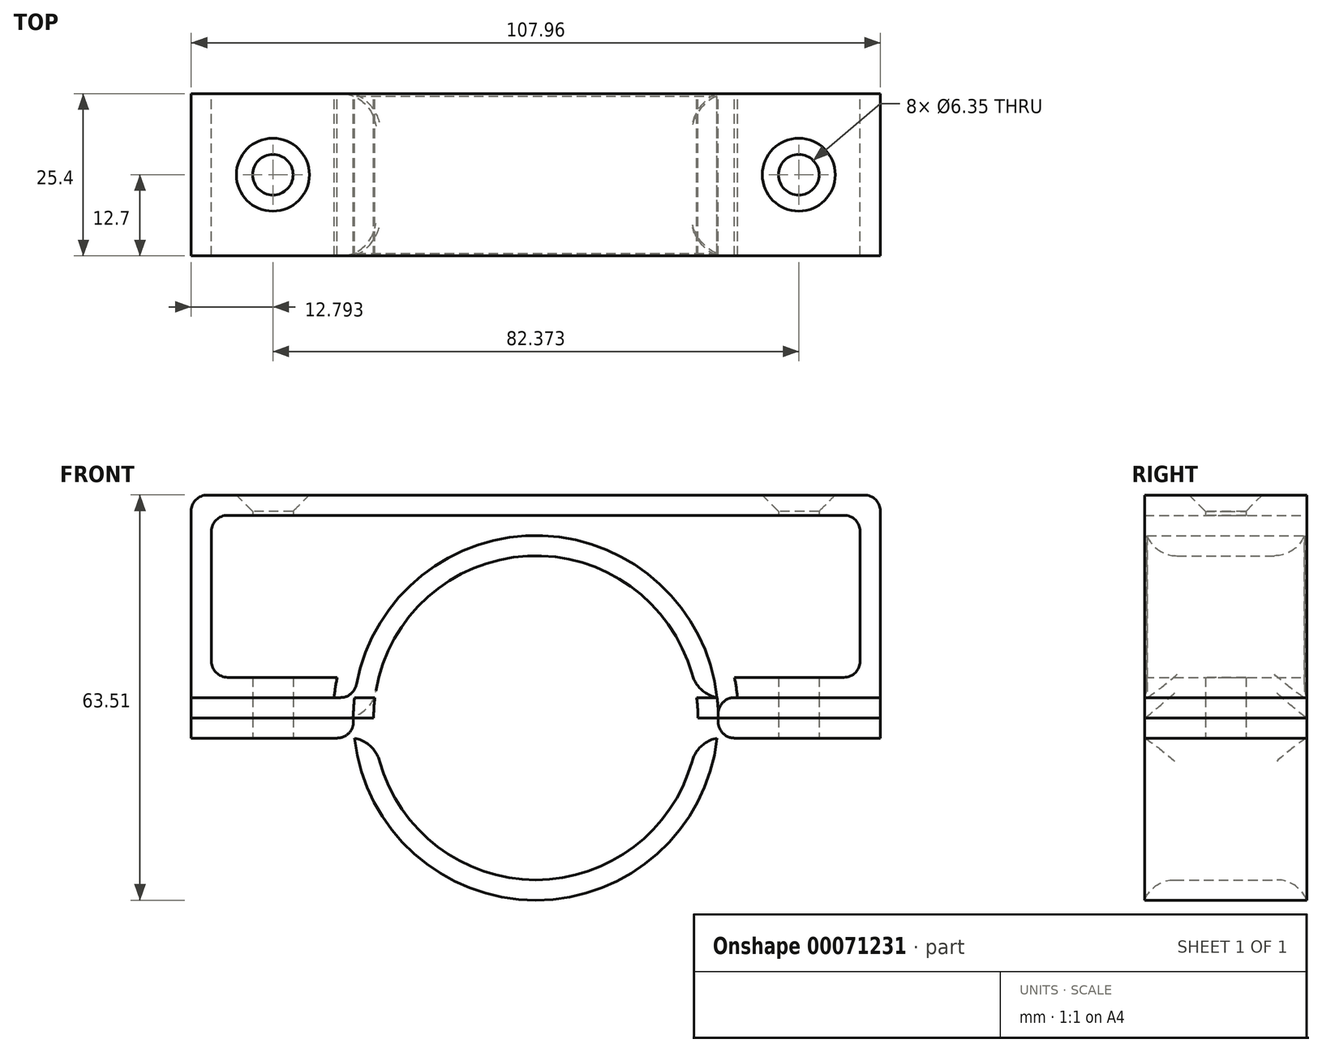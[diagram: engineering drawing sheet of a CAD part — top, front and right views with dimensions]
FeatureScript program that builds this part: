
annotation { "Feature Type Name" : "Feature", "Feature Type Description" : "" }
export const myFeature = defineFeature(function(context is Context, id is Id, definition is map)
    precondition{}
    {
        {
            var Q0;
            Q0=qCreatedBy(makeId("Front.planeOp"),FACE);
            var sketch = newSketch(context, id + "F0", { "sketchPlane" : qUnion([Q0])});
            skCircle(sketch, "E0", {"center": v(0, 0) * mm, "radius": 25.4 * mm});
            skLineSegment(sketch, "E1", {"start": v(-53.98, 0) * mm, "end": v(53.98, 0) * mm});
            skCircle(sketch, "E2.0", {"center": v(0, 0) * mm, "radius": 28.58 * mm});
            skLineSegment(sketch, "E3", {"start": v(-53.98, 3.18) * mm, "end": v(53.98, 3.18) * mm});
            skLineSegment(sketch, "E4", {"start": v(-53.98, -3.18) * mm, "end": v(53.98, -3.18) * mm});
            skLineSegment(sketch, "E5", {"start": v(-53.98, 3.18) * mm, "end": v(-53.98, -3.18) * mm});
            skLineSegment(sketch, "E6", {"start": v(53.98, 3.18) * mm, "end": v(53.98, -3.18) * mm});
            skSolve(sketch);
        }
        {
            var Q0;
            {var subQ0=sQuery(id+"F0.wireOp",EDGE,"E5");var subQ1=sQuery(id+"F0.wireOp",EDGE,"E1");var subQ2=makeQuery(id+"F0.imprint","INTERSECT",VERTEX,{"derivedFrom":[subQ1,subQ0]});Q0=makeQuery(id+"F0.imprint","IMPRINT",FACE,{"disambiguationData":[TD([[makeQuery(id+"F0.imprint","IMPRINT",EDGE,{"disambiguationData":[TD([[subQ2,-1.0]])],"derivedFrom":subQ1}),1.0]])]});}
            var Q1;
            {var subQ0=sQuery(id+"F0.wireOp",EDGE,"E3");var subQ1=sQuery(id+"F0.wireOp",EDGE,"E0");var subQ2=makeQuery(id+"F0.imprint","INTERSECT",VERTEX,{"disambiguationData":[OD(1.0)],"derivedFrom":[subQ1,subQ0]});Q1=makeQuery(id+"F0.imprint","IMPRINT",FACE,{"disambiguationData":[TD([[makeQuery(id+"F0.imprint","IMPRINT",EDGE,{"disambiguationData":[TD([[subQ2,-1.0]])],"derivedFrom":subQ1}),-1.0]])]});}
            var Q2;
            {var subQ0=sQuery(id+"F0.wireOp",EDGE,"E3");var subQ1=sQuery(id+"F0.wireOp",EDGE,"E0");var subQ2=makeQuery(id+"F0.imprint","INTERSECT",VERTEX,{"disambiguationData":[OD(0.0)],"derivedFrom":[subQ1,subQ0]});Q2=makeQuery(id+"F0.imprint","IMPRINT",FACE,{"disambiguationData":[TD([[makeQuery(id+"F0.imprint","IMPRINT",EDGE,{"disambiguationData":[TD([[subQ2,-1.0]])],"derivedFrom":subQ1}),-1.0]])]});}
            var Q3;
            {var subQ0=sQuery(id+"F0.wireOp",EDGE,"E3");var subQ1=sQuery(id+"F0.wireOp",EDGE,"E0");var subQ2=makeQuery(id+"F0.imprint","INTERSECT",VERTEX,{"disambiguationData":[OD(0.0)],"derivedFrom":[subQ1,subQ0]});Q3=makeQuery(id+"F0.imprint","IMPRINT",FACE,{"disambiguationData":[TD([[makeQuery(id+"F0.imprint","IMPRINT",EDGE,{"disambiguationData":[TD([[subQ2,1.0]])],"derivedFrom":subQ1}),-1.0]])]});}
            var Q4;
            {var subQ0=sQuery(id+"F0.wireOp",EDGE,"E6");var subQ1=sQuery(id+"F0.wireOp",EDGE,"E1");var subQ2=makeQuery(id+"F0.imprint","INTERSECT",VERTEX,{"derivedFrom":[subQ1,subQ0]});Q4=makeQuery(id+"F0.imprint","IMPRINT",FACE,{"disambiguationData":[TD([[makeQuery(id+"F0.imprint","IMPRINT",EDGE,{"disambiguationData":[TD([[subQ2,1.0]])],"derivedFrom":subQ1}),1.0]])]});}
            extrude(context, id + "F1", {"entities" : qUnion([Q0, Q1, Q2, Q3, Q4]), "depth" : 25.4 * mm});
        }
        {
            var Q0;
            {var subQ0=sQuery(id+"F0.wireOp",EDGE,"E5");var subQ1=sQuery(id+"F0.wireOp",EDGE,"E1");var subQ2=makeQuery(id+"F0.imprint","INTERSECT",VERTEX,{"derivedFrom":[subQ1,subQ0]});Q0=makeQuery(id+"F0.imprint","IMPRINT",FACE,{"disambiguationData":[TD([[makeQuery(id+"F0.imprint","IMPRINT",EDGE,{"disambiguationData":[TD([[subQ2,-1.0]])],"derivedFrom":subQ1}),-1.0]])]});}
            var Q1;
            {var subQ0=sQuery(id+"F0.wireOp",EDGE,"E1");var subQ1=sQuery(id+"F0.wireOp",EDGE,"E0");var subQ2=makeQuery(id+"F0.imprint","INTERSECT",VERTEX,{"disambiguationData":[OD(1.0)],"derivedFrom":[subQ1,subQ0]});Q1=makeQuery(id+"F0.imprint","IMPRINT",FACE,{"disambiguationData":[TD([[makeQuery(id+"F0.imprint","IMPRINT",EDGE,{"disambiguationData":[TD([[subQ2,-1.0]])],"derivedFrom":subQ1}),-1.0]])]});}
            var Q2;
            {var subQ0=sQuery(id+"F0.wireOp",EDGE,"E4");var subQ1=sQuery(id+"F0.wireOp",EDGE,"E0");var subQ2=makeQuery(id+"F0.imprint","INTERSECT",VERTEX,{"disambiguationData":[OD(0.0)],"derivedFrom":[subQ1,subQ0]});Q2=makeQuery(id+"F0.imprint","IMPRINT",FACE,{"disambiguationData":[TD([[makeQuery(id+"F0.imprint","IMPRINT",EDGE,{"disambiguationData":[TD([[subQ2,-1.0]])],"derivedFrom":subQ1}),-1.0]])]});}
            var Q3;
            {var subQ0=sQuery(id+"F0.wireOp",EDGE,"E1");var subQ1=sQuery(id+"F0.wireOp",EDGE,"E0");var subQ2=makeQuery(id+"F0.imprint","INTERSECT",VERTEX,{"disambiguationData":[OD(0.0)],"derivedFrom":[subQ1,subQ0]});Q3=makeQuery(id+"F0.imprint","IMPRINT",FACE,{"disambiguationData":[TD([[makeQuery(id+"F0.imprint","IMPRINT",EDGE,{"disambiguationData":[TD([[subQ2,1.0]])],"derivedFrom":subQ1}),-1.0]])]});}
            var Q4;
            {var subQ0=sQuery(id+"F0.wireOp",EDGE,"E6");var subQ1=sQuery(id+"F0.wireOp",EDGE,"E1");var subQ2=makeQuery(id+"F0.imprint","INTERSECT",VERTEX,{"derivedFrom":[subQ1,subQ0]});Q4=makeQuery(id+"F0.imprint","IMPRINT",FACE,{"disambiguationData":[TD([[makeQuery(id+"F0.imprint","IMPRINT",EDGE,{"disambiguationData":[TD([[subQ2,1.0]])],"derivedFrom":subQ1}),-1.0]])]});}
            extrude(context, id + "F2", {"entities" : qUnion([Q0, Q1, Q2, Q3, Q4]), "depth" : 25.4 * mm});
        }
        {
            var Q0;
            {var subQ0=sQuery(id+"F0.wireOp",EDGE,"E4");Q0=makeQuery(id+"F2.opExtrude","SWEPT_FACE",FACE,{"disambiguationData":[OSD([subQ0]),TDD([makeQuery(id+"F0.imprint","IMPRINT",EDGE,{"disambiguationData":[TD([[makeQuery(id+"F0.imprint","INTERSECT",VERTEX,{"derivedFrom":[subQ0,sQuery(id+"F0.wireOp",EDGE,"E5")]}),-1.0]])],"derivedFrom":subQ0})])]});}
            var sketch = newSketch(context, id + "F3", { "sketchPlane" : qUnion([Q0])});
            skLineSegment(sketch, "E7.0", {"start": v(-53.98, 25.4) * mm, "end": v(-28.4, 25.4) * mm});
            skLineSegment(sketch, "E7.1", {"start": v(-53.98, 25.4) * mm, "end": v(-53.98, 0) * mm});
            skLineSegment(sketch, "E7.2", {"start": v(-53.98, 0) * mm, "end": v(53.98, 0) * mm});
            skLineSegment(sketch, "E7.3", {"start": v(-28.4, 25.4) * mm, "end": v(-28.4, 0) * mm});
            skLineSegment(sketch, "E7.4", {"start": v(28.4, 25.4) * mm, "end": v(53.98, 25.4) * mm});
            skLineSegment(sketch, "E7.5", {"start": v(53.98, 25.4) * mm, "end": v(53.98, 0) * mm});
            skLineSegment(sketch, "E7.6", {"start": v(28.4, 25.4) * mm, "end": v(28.4, 0) * mm});
            skLineSegment(sketch, "E8", {"start": v(-53.98, 0) * mm, "end": v(-28.4, 25.4) * mm, "construction": true});
            skLineSegment(sketch, "E9", {"start": v(28.4, 25.4) * mm, "end": v(53.97, 0) * mm, "construction": true});
            skCircle(sketch, "E10", {"center": v(-41.19, 12.7) * mm, "radius": 3.18 * mm});
            skCircle(sketch, "E11", {"center": v(41.19, 12.7) * mm, "radius": 3.18 * mm});
            skSolve(sketch);
        }
        {
            var Q0;
            Q0=makeQuery(id+"F1.opExtrude","SWEPT_FACE",FACE,{"disambiguationData":[OSD([sQuery(id+"F0.wireOp",EDGE,"E0")])]});
            var Q1;
            Q1=makeQuery(id+"F2.opExtrude","SWEPT_FACE",FACE,{"disambiguationData":[OSD([sQuery(id+"F0.wireOp",EDGE,"E0")])]});
            fillet(context, id + "F4", {"entities" : qUnion([Q0, Q1]), "radius" : 5.08 * mm, "tangentPropagation" : true, "allowEdgeOverflow" : false});
        }
        {
            var Q0;
            {var subQ0=sQuery(id+"F0.wireOp",EDGE,"E3");var subQ1=sQuery(id+"F0.wireOp",EDGE,"E2.0");Q0=makeQuery(id+"F1.opExtrude","SWEPT_EDGE",EDGE,{"disambiguationData":[OSD([subQ1,subQ0]),TDD([makeQuery(id+"F0.imprint","INTERSECT",VERTEX,{"disambiguationData":[OD(1.0)],"derivedFrom":[subQ1,subQ0]})])]});}
            var Q1;
            {var subQ0=sQuery(id+"F0.wireOp",EDGE,"E4");var subQ1=sQuery(id+"F0.wireOp",EDGE,"E2.0");Q1=makeQuery(id+"F2.opExtrude","SWEPT_EDGE",EDGE,{"disambiguationData":[OSD([subQ1,subQ0]),TDD([makeQuery(id+"F0.imprint","INTERSECT",VERTEX,{"disambiguationData":[OD(0.0)],"derivedFrom":[subQ1,subQ0]})])]});}
            var Q2;
            {var subQ0=sQuery(id+"F0.wireOp",EDGE,"E4");var subQ1=sQuery(id+"F0.wireOp",EDGE,"E2.0");Q2=makeQuery(id+"F2.opExtrude","SWEPT_EDGE",EDGE,{"disambiguationData":[OSD([subQ1,subQ0]),TDD([makeQuery(id+"F0.imprint","INTERSECT",VERTEX,{"disambiguationData":[OD(1.0)],"derivedFrom":[subQ1,subQ0]})])]});}
            var Q3;
            {var subQ0=sQuery(id+"F0.wireOp",EDGE,"E3");var subQ1=sQuery(id+"F0.wireOp",EDGE,"E2.0");Q3=makeQuery(id+"F1.opExtrude","SWEPT_EDGE",EDGE,{"disambiguationData":[OSD([subQ1,subQ0]),TDD([makeQuery(id+"F0.imprint","INTERSECT",VERTEX,{"disambiguationData":[OD(0.0)],"derivedFrom":[subQ1,subQ0]})])]});}
            fillet(context, id + "F5", {"entities" : qUnion([Q0, Q1, Q2, Q3]), "radius" : 2.54 * mm, "tangentPropagation" : true, "allowEdgeOverflow" : false});
        }
        {
            var Q0;
            Q0=qCreatedBy(makeId("Front.planeOp"),FACE);
            var sketch = newSketch(context, id + "F6", { "sketchPlane" : qUnion([Q0])});
            skLineSegment(sketch, "E12.0", {"start": v(-53.98, -3.18) * mm, "end": v(53.98, -3.18) * mm});
            skLineSegment(sketch, "E12.1", {"start": v(-53.98, 3.18) * mm, "end": v(53.98, 3.18) * mm});
            skCircle(sketch, "E12.2", {"center": v(0, 0) * mm, "radius": 28.58 * mm});
            skLineSegment(sketch, "E13", {"start": v(-53.98, 3.18) * mm, "end": v(-53.98, 34.93) * mm});
            skLineSegment(sketch, "E14", {"start": v(-53.98, 34.93) * mm, "end": v(53.98, 34.93) * mm});
            skLineSegment(sketch, "E15", {"start": v(53.98, 34.93) * mm, "end": v(53.98, 3.18) * mm});
            skCircle(sketch, "E16", {"center": v(0, 0) * mm, "radius": 31.75 * mm});
            skLineSegment(sketch, "E17", {"start": v(31.1, 6.35) * mm, "end": v(53.98, 6.35) * mm});
            skLineSegment(sketch, "E18", {"start": v(-53.98, 6.35) * mm, "end": v(-31.1, 6.35) * mm});
            skLineSegment(sketch, "E19", {"start": v(-53.98, 31.75) * mm, "end": v(53.98, 31.75) * mm});
            skLineSegment(sketch, "E20", {"start": v(-50.8, 6.35) * mm, "end": v(-50.8, 31.75) * mm});
            skLineSegment(sketch, "E21", {"start": v(50.8, 6.35) * mm, "end": v(50.8, 31.75) * mm});
            skArc(sketch, "E22.0", {"start": v(-30.31, 3.19) * mm, "mid": v(-28.86, 3.85) * mm, "end": v(-28.09, 5.25) * mm});
            skArc(sketch, "E22.1", {"start": v(28.09, 5.25) * mm, "mid": v(28.86, 3.85) * mm, "end": v(30.31, 3.19) * mm});
            skArc(sketch, "E23.0", {"start": v(-28.09, 5.25) * mm, "mid": v(-28.86, 3.85) * mm, "end": v(-30.31, 3.19) * mm});
            skSolve(sketch);
        }
        {
            var Q0;
            {var subQ1=sQuery(id+"F6.wireOp",EDGE,"E13");var subQ6=sQuery(id+"F6.wireOp",EDGE,"E12.1");var subQ8=makeQuery(id+"F6.imprint","INTERSECT",VERTEX,{"derivedFrom":[subQ6,subQ1]});Q0=makeQuery(id+"F6.imprint","IMPRINT",FACE,{"disambiguationData":[TD([[makeQuery(id+"F6.imprint","IMPRINT",EDGE,{"disambiguationData":[TD([[subQ8,-1.0]])],"derivedFrom":subQ6}),1.0]])]});}
            var Q1;
            {var subQ5=sQuery(id+"F6.wireOp",EDGE,"E20");Q1=makeQuery(id+"F6.imprint","IMPRINT",FACE,{"disambiguationData":[TD([[makeQuery(id+"F6.imprint","IMPRINT",EDGE,{"derivedFrom":subQ5}),1.0]])]});}
            var Q2;
            {var subQ5=sQuery(id+"F6.wireOp",EDGE,"E14");Q2=makeQuery(id+"F6.imprint","IMPRINT",FACE,{"disambiguationData":[TD([[makeQuery(id+"F6.imprint","IMPRINT",EDGE,{"derivedFrom":subQ5}),-1.0]])]});}
            var Q3;
            {var subQ5=sQuery(id+"F6.wireOp",EDGE,"E21");Q3=makeQuery(id+"F6.imprint","IMPRINT",FACE,{"disambiguationData":[TD([[makeQuery(id+"F6.imprint","IMPRINT",EDGE,{"derivedFrom":subQ5}),-1.0]])]});}
            var Q4;
            {var subQ3=sQuery(id+"F6.wireOp",EDGE,"E12.1");var subQ5=sQuery(id+"F6.wireOp",EDGE,"E15");var subQ6=makeQuery(id+"F6.imprint","INTERSECT",VERTEX,{"derivedFrom":[subQ3,subQ5]});Q4=makeQuery(id+"F6.imprint","IMPRINT",FACE,{"disambiguationData":[TD([[makeQuery(id+"F6.imprint","IMPRINT",EDGE,{"disambiguationData":[TD([[subQ6,1.0]])],"derivedFrom":subQ3}),1.0]])]});}
            extrude(context, id + "F7", {"entities" : qUnion([Q0, Q1, Q2, Q3, Q4]), "depth" : 25.4 * mm});
        }
        {
            var Q0;
            Q0=makeQuery(id+"F7.opExtrude","SWEPT_EDGE",EDGE,{"disambiguationData":[OSD([sQuery(id+"F6.wireOp",EDGE,"E18"),sQuery(id+"F6.wireOp",EDGE,"E20")])]});
            var Q1;
            Q1=makeQuery(id+"F7.opExtrude","SWEPT_EDGE",EDGE,{"disambiguationData":[OSD([sQuery(id+"F6.wireOp",EDGE,"E17"),sQuery(id+"F6.wireOp",EDGE,"E21")])]});
            var Q2;
            Q2=makeQuery(id+"F7.opExtrude","SWEPT_EDGE",EDGE,{"disambiguationData":[OSD([sQuery(id+"F6.wireOp",EDGE,"E19"),sQuery(id+"F6.wireOp",EDGE,"E21")])]});
            var Q3;
            Q3=makeQuery(id+"F7.opExtrude","SWEPT_EDGE",EDGE,{"disambiguationData":[OSD([sQuery(id+"F6.wireOp",EDGE,"E19"),sQuery(id+"F6.wireOp",EDGE,"E20")])]});
            var Q4;
            Q4=makeQuery(id+"F7.opExtrude","SWEPT_EDGE",EDGE,{"disambiguationData":[OSD([sQuery(id+"F6.wireOp",EDGE,"E14"),sQuery(id+"F6.wireOp",EDGE,"E15")])]});
            var Q5;
            Q5=makeQuery(id+"F7.opExtrude","SWEPT_EDGE",EDGE,{"disambiguationData":[OSD([sQuery(id+"F6.wireOp",EDGE,"E13"),sQuery(id+"F6.wireOp",EDGE,"E14")])]});
            fillet(context, id + "F8", {"entities" : qUnion([Q0, Q1, Q2, Q3, Q4, Q5]), "radius" : 2.54 * mm, "tangentPropagation" : true, "allowEdgeOverflow" : false});
        }
        {
            var Q0;
            Q0=makeQuery(id+"F3.imprint","IMPRINT",FACE,{"disambiguationData":[TD([[makeQuery(id+"F3.imprint","IMPRINT",EDGE,{"derivedFrom":sQuery(id+"F3.wireOp",EDGE,"E10")}),1.0]])]});
            var Q1;
            Q1=makeQuery(id+"F3.imprint","IMPRINT",FACE,{"disambiguationData":[TD([[makeQuery(id+"F3.imprint","IMPRINT",EDGE,{"derivedFrom":sQuery(id+"F3.wireOp",EDGE,"E11")}),1.0]])]});
            extrude(context, id + "F9", {"entities" : qUnion([Q0, Q1]), "operationType" : NewBodyOperationType.REMOVE, "endBound" : BoundingType.THROUGH_ALL, "oppositeDirection" : true, "depth" : 25.4 * mm});
        }
        {
            var Q0;
            Q0=makeQuery(id+"F9.boolean.opBoolean","INTERSECT",EDGE,{"derivedFrom":[makeQuery(id+"F7.opExtrude","SWEPT_FACE",FACE,{"disambiguationData":[OSD([sQuery(id+"F6.wireOp",EDGE,"E14")])]}),makeQuery(id+"F9.opExtrude","SWEPT_FACE",FACE,{"disambiguationData":[OSD([sQuery(id+"F3.wireOp",EDGE,"E10")])]})]});
            var Q1;
            Q1=makeQuery(id+"F9.boolean.opBoolean","INTERSECT",EDGE,{"derivedFrom":[makeQuery(id+"F7.opExtrude","SWEPT_FACE",FACE,{"disambiguationData":[OSD([sQuery(id+"F6.wireOp",EDGE,"E14")])]}),makeQuery(id+"F9.opExtrude","SWEPT_FACE",FACE,{"disambiguationData":[OSD([sQuery(id+"F3.wireOp",EDGE,"E11")])]})]});
            var Q2;
            Q2=makeQuery(id+"F9.boolean.opBoolean","COPY",EDGE,{"derivedFrom":makeQuery(id+"F9.opExtrude","CAP_EDGE",EDGE,{"disambiguationData":[OSD([sQuery(id+"F3.wireOp",EDGE,"E10")])],"isStart":true})});
            var Q3;
            Q3=makeQuery(id+"F9.boolean.opBoolean","COPY",EDGE,{"derivedFrom":makeQuery(id+"F9.opExtrude","CAP_EDGE",EDGE,{"disambiguationData":[OSD([sQuery(id+"F3.wireOp",EDGE,"E11")])],"isStart":true})});
            chamfer(context, id + "F10", {"entities" : qUnion([Q0, Q1, Q2, Q3]), "width" : 2.54 * mm, "tangentPropagation" : true});
        }
    });
